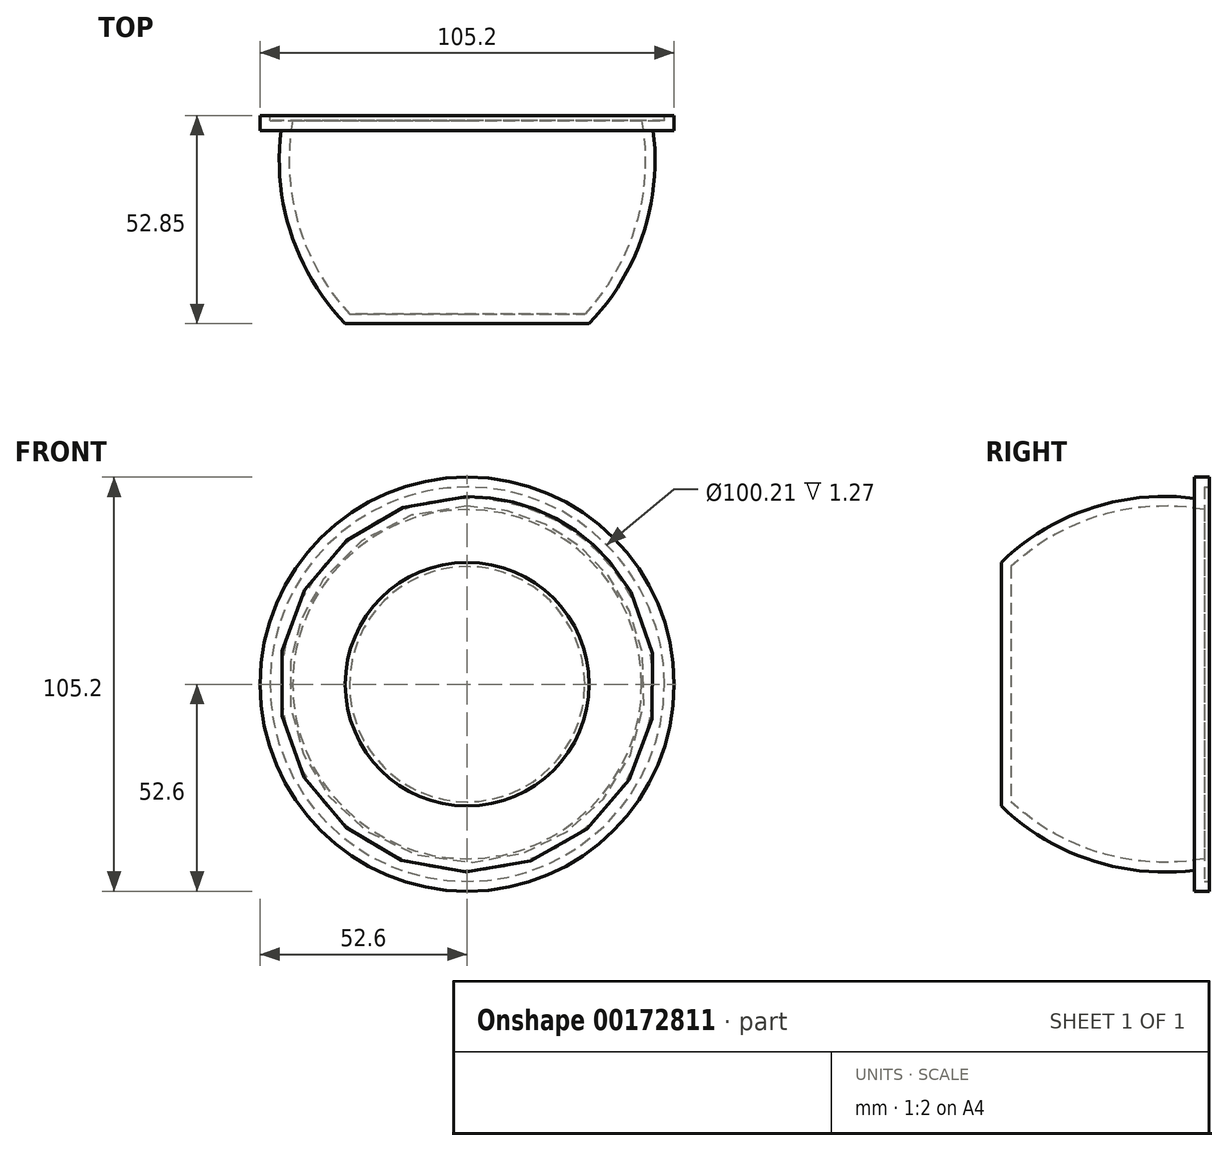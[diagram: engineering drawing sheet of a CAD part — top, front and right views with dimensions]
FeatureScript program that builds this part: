
annotation { "Feature Type Name" : "Feature", "Feature Type Description" : "" }
export const myFeature = defineFeature(function(context is Context, id is Id, definition is map)
    precondition{}
    {
        {
            var Q0;
            Q0=qCreatedBy(makeId("Top.planeOp"),FACE);
            var sketch = newSketch(context, id + "F0", { "sketchPlane" : qUnion([Q0])});
            skLineSegment(sketch, "E0", {"start": v(0, 0) * mm, "end": v(30.95, 0) * mm});
            skArc(sketch, "E1", {"start": v(30.95, 0) * mm, "mid": v(44.69, 22.69) * mm, "end": v(47.25, 49.08) * mm});
            skLineSegment(sketch, "E2.bottom", {"start": v(47.25, 49.08) * mm, "end": v(52.6, 49.08) * mm});
            skLineSegment(sketch, "E2.top", {"start": v(47.25, 52.85) * mm, "end": v(52.6, 52.85) * mm});
            skLineSegment(sketch, "E2.right", {"start": v(52.6, 49.08) * mm, "end": v(52.6, 52.85) * mm});
            skLineSegment(sketch, "E3", {"start": v(47.25, 52.85) * mm, "end": v(0, 52.85) * mm});
            skLineSegment(sketch, "E4", {"start": v(0, 52.85) * mm, "end": v(0, 0) * mm});
            skSolve(sketch);
        }
        {
            var Q0;
            Q0=makeQuery(id+"F0.imprint","IMPRINT",FACE,{"disambiguationData":[TD([[makeQuery(id+"F0.imprint","IMPRINT",EDGE,{"derivedFrom":sQuery(id+"F0.wireOp",EDGE,"E0")}),1.0]])]});
            var Q1;
            Q1=sQuery(id+"F0.wireOp",EDGE,"E4");
            revolve(context, id + "F1", {"entities" : qUnion([Q0]), "axis" : qUnion([Q1]), "revolveType" : RevolveType.FULL});
        }
        {
            var Q0;
            Q0=makeQuery(id+"F1.opRevolve","SWEPT_FACE",FACE,{"disambiguationData":[OSD([sQuery(id+"F0.wireOp",EDGE,"E2.top"),sQuery(id+"F0.wireOp",EDGE,"E3")])]});
            shell(context, id + "F2", {"entities" : qUnion([Q0]), "thickness" : 2.5 * mm});
        }
    });
